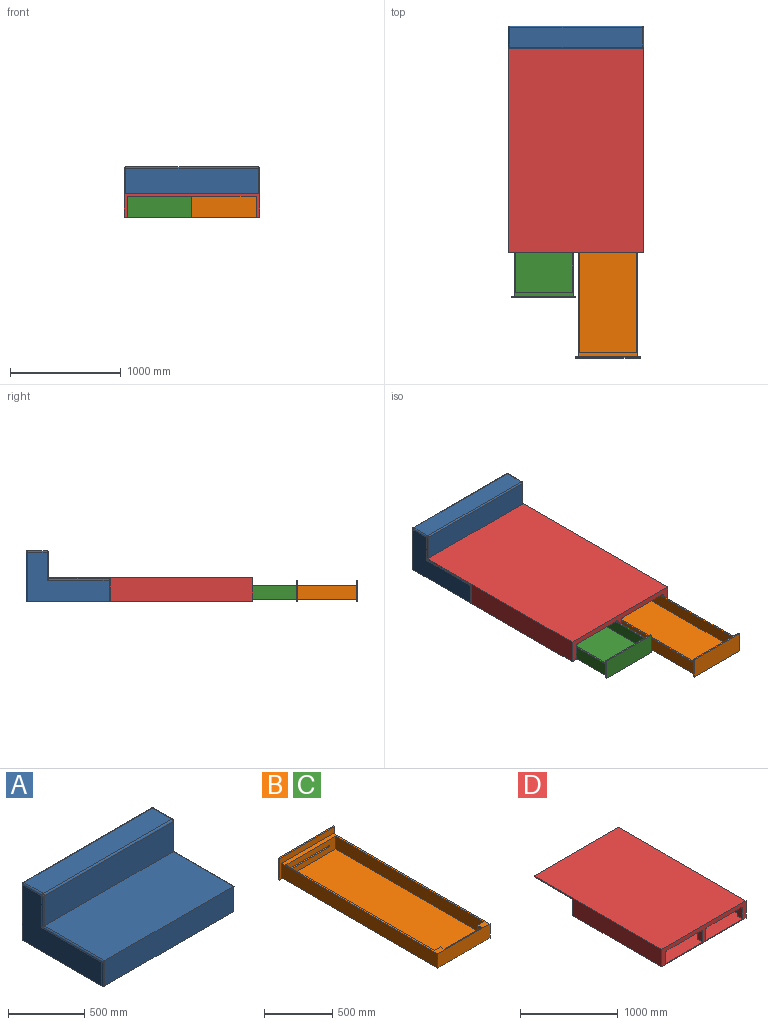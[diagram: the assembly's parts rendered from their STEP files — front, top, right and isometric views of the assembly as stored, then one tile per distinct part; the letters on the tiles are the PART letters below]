
ASSEMBLY  parts=4 mates=6
PART A: 24 faces, bbox 1219.2x762x457.2 mm
  f0: plane 1219.2x762mm, normal (0,0,-1), area 928891.9mm2, adj f1,f5,f6,f7,f8,f9,f17,f20
  f1: plane 1193.8x444.5mm, normal (0,1,0), area 530644.1mm2, adj f0,f17,f20,f23
  f2: plane 1193.8x177.8mm, normal (0,0,1), area 212257.6mm2, adj f13,f18,f19,f23
  f3: plane 1193.8x241.3mm, normal (0,-1,0), area 288063.9mm2, adj f4,f12,f13,f14
  f4: plane 1193.8x558.8mm, normal (0,0,1), area 667095.4mm2, adj f3,f5,f10,f11
  f5: plane 1193.8x203.2mm, normal (0,-1,0), area 242580.2mm2, adj f0,f4,f8,f9
  f6: plane 736.6x444.5mm, normal (1,0,0), area 185483.5mm2, adj f0,f8,f10,f12,f17,f18
  f7: plane 736.6x444.5mm, normal (-1,0,0), area 185483.5mm2, adj f0,f9,f11,f14,f19,f20
  f8: cylinder r=12.7mm len=203.2mm, axis (0,0,1), area 3961.6mm2, adj f0,f5,f6,f10
  f9: cylinder r=12.7mm len=203.2mm, axis (0,0,-1), area 3961.6mm2, adj f0,f5,f7,f11
  f10: cylinder r=12.7mm len=571.5mm, axis (0,1,0), area 11147.6mm2, adj f4,f6,f8,f12
  f11: cylinder r=12.7mm len=571.5mm, axis (0,-1,0), area 11147.6mm2, adj f4,f7,f9,f14
  f12: cylinder r=12.7mm len=254mm, axis (0,0,1), area 4905.8mm2, adj f3,f6,f10,f15
  f13: cylinder r=12.7mm len=1193.8mm, axis (-1,0,0), area 23815.3mm2, adj f2,f3,f15,f16
  f14: cylinder r=12.7mm len=254mm, axis (0,0,-1), area 4905.8mm2, adj f3,f7,f11,f16
  f15: sphere r=12.7mm, area 253.4mm2, adj f12,f13,f18
  f16: sphere r=12.7mm, area 253.4mm2, adj f13,f14,f19
  f17: cylinder r=12.7mm len=444.5mm, axis (0,0,-1), area 8867.4mm2, adj f0,f1,f6,f21
  f18: cylinder r=12.7mm len=177.8mm, axis (0,1,0), area 3547mm2, adj f2,f6,f15,f21
  f19: cylinder r=12.7mm len=177.8mm, axis (0,-1,0), area 3547mm2, adj f2,f7,f16,f22
  f20: cylinder r=12.7mm len=444.5mm, axis (0,0,1), area 8867.4mm2, adj f0,f1,f7,f22
  f21: sphere r=12.7mm, area 253.4mm2, adj f17,f18,f23
  f22: sphere r=12.7mm, area 253.4mm2, adj f19,f20,f23
  f23: cylinder r=12.7mm len=1193.8mm, axis (-1,0,0), area 23815.3mm2, adj f1,f2,f21,f22
PART B: 25 faces, bbox 577.9x1638.3x190.5 mm
  f0: plane 1574.8x514.35mm, normal (0,0,1), area 805159.7mm2, adj f14,f15,f16,f17,f18,f19,f20,f21
  f1: plane 38.1x12.7mm, normal (-1,0,0), area 483.9mm2, adj f4,f14,f23,f24
  f2: plane 38.1x12.7mm, normal (1,0,0), area 483.9mm2, adj f4,f14,f23,f24
  f3: plane 577.85x190.5mm, normal (0,-1,0), area 41532.2mm2, adj f5,f6,f7,f8,f11,f12,f13,f22
  f4: plane 387.35x12.7mm, normal (0,-1,0), area 4919.3mm2, adj f1,f2,f23,f24
  f5: plane 577.85x12.7mm, normal (0,0,1), area 7338.7mm2, adj f3,f6,f8,f9
  f6: plane 190.5x12.7mm, normal (1,0,0), area 2419.4mm2, adj f3,f5,f7,f9
  f7: plane 577.85x12.7mm, normal (0,0,-1), area 7338.7mm2, adj f3,f6,f8,f9
  f8: plane 190.5x12.7mm, normal (-1,0,0), area 2419.4mm2, adj f3,f5,f7,f9
  f9: plane 577.85x190.5mm, normal (0,1,0), area 110080.4mm2, adj f5,f6,f7,f8
  f10: plane 539.75x127mm, normal (0,-1,0), area 68548.2mm2, adj f11,f12,f13,f22
  f11: plane 1625.6x127mm, normal (1,0,0), area 206451.2mm2, adj f3,f10,f13,f22
  f12: plane 1625.6x127mm, normal (-1,0,0), area 206451.2mm2, adj f3,f10,f13,f22
  f13: plane 1625.6x539.75mm, normal (0,0,-1), area 877417.6mm2, adj f3,f10,f11,f12
  f14: plane 514.35x114.3mm, normal (0,-1,0), area 53870.9mm2, adj f0,f1,f2,f15,f21,f22,f23,f24
  f15: plane 1536.7x114.3mm, normal (-1,0,0), area 175644.8mm2, adj f0,f14,f16,f22
  f16: plane 114.3x63.5mm, normal (0,1,0), area 7258.1mm2, adj f0,f15,f17,f22
  f17: plane 114.3x38.1mm, normal (-1,0,0), area 4354.8mm2, adj f0,f16,f18,f22
  f18: plane 387.35x114.3mm, normal (0,1,0), area 44274.1mm2, adj f0,f17,f19,f22
  f19: plane 114.3x38.1mm, normal (1,0,0), area 4354.8mm2, adj f0,f18,f20,f22
  f20: plane 114.3x63.5mm, normal (0,1,0), area 7258mm2, adj f0,f19,f21,f22
  f21: plane 1536.7x114.3mm, normal (1,0,0), area 175644.8mm2, adj f0,f14,f20,f22
  f22: plane 1625.6x539.75mm, normal (0,0,1), area 72257.9mm2, adj f3,f10,f11,f12,f14,f15,f16,f17
  f23: plane 387.35x38.1mm, normal (0,0,-1), area 14758mm2, adj f1,f2,f4,f14
  f24: plane 387.35x38.1mm, normal (0,0,1), area 14758mm2, adj f1,f2,f4,f14
PART C: same geometry as B
PART D: 64 faces, bbox 1219.2x1841.5x215.9 mm
  f0: plane 1104.9x127mm, normal (-1,0,0), area 140322.3mm2, adj f1,f4,f22,f47
  f1: plane 127x38.1mm, normal (0,-1,0), area 4838.7mm2, adj f0,f3,f22,f47
  f2: plane 539.75x152.4mm, normal (0,-1,0), area 82257.9mm2, adj f3,f5,f21,f47
  f3: plane 1270x190.5mm, normal (-1,0,0), area 91357.7mm2, adj f1,f2,f4,f17,f21,f22,f28,f29
  f4: plane 127x38.1mm, normal (0,1,0), area 4838.7mm2, adj f0,f3,f22,f47
  f5: plane 1270x190.5mm, normal (1,0,0), area 91357.7mm2, adj f2,f6,f7,f14,f20,f21,f24,f25
  f6: plane 127x38.1mm, normal (0,-1,0), area 4838.7mm2, adj f5,f13,f14,f47
  f7: plane 127x38.1mm, normal (0,1,0), area 4838.7mm2, adj f5,f13,f14,f47
  f8: plane 1104.9x127mm, normal (1,0,0), area 140322.3mm2, adj f9,f12,f38,f47
  f9: plane 127x38.1mm, normal (0,-1,0), area 4838.7mm2, adj f8,f11,f38,f47
  f10: plane 539.75x152.4mm, normal (0,-1,0), area 82257.9mm2, adj f11,f13,f37,f47
  f11: plane 1270x190.5mm, normal (1,0,0), area 91357.7mm2, adj f9,f10,f12,f33,f37,f38,f44,f45
  f12: plane 127x38.1mm, normal (0,1,0), area 4838.7mm2, adj f8,f11,f38,f47
  f13: plane 1270x190.5mm, normal (-1,0,0), area 91357.7mm2, adj f6,f7,f10,f14,f36,f37,f40,f41
  f14: plane 1104.9x38.1mm, normal (0,0,-1), area 42096.7mm2, adj f5,f6,f7,f13
  f15: plane 477.2x444.16mm, normal (0,0,-1), area 105976mm2, adj f19,f23,f30
  f16: plane 477.2x444.16mm, normal (0,0,-1), area 105976mm2, adj f18,f26,f27
  f17: plane 1009.31x234.86mm, normal (0,0,-1), area 118520.6mm2, adj f3,f28,f29
  f18: plane 444.16x38.1mm, normal (0,-1,0), area 16922.4mm2, adj f16,f21,f26,f27
  f19: plane 444.16x38.1mm, normal (0,1,0), area 16922.4mm2, adj f15,f21,f23,f30
  f20: plane 1009.31x234.86mm, normal (0,0,-1), area 118520.6mm2, adj f5,f24,f25
  f21: plane 1270x539.75mm, normal (0,0,-1), area 235844.3mm2, adj f2,f3,f5,f18,f19,f23,f24,f25
  f22: plane 1104.9x38.1mm, normal (0,0,-1), area 42096.7mm2, adj f0,f1,f3,f4
  f23: plane 477.2x222.08mm, normal (0.91,-0.42,0), area 20053.7mm2, adj f15,f19,f21,f30
  f24: plane 504.65x234.86mm, normal (-0.91,0.42,0), area 21207.4mm2, adj f5,f20,f21,f25
  f25: plane 504.65x234.86mm, normal (-0.91,-0.42,0), area 21207.4mm2, adj f5,f20,f21,f24
  f26: plane 477.2x222.08mm, normal (0.91,0.42,0), area 20053.7mm2, adj f16,f18,f21,f27
  f27: plane 477.2x222.08mm, normal (-0.91,0.42,0), area 20053.7mm2, adj f16,f18,f21,f26
  f28: plane 504.65x234.86mm, normal (0.91,-0.42,0), area 21207.4mm2, adj f3,f17,f21,f29
  f29: plane 504.65x234.86mm, normal (0.91,0.42,0), area 21207.4mm2, adj f3,f17,f21,f28
  f30: plane 477.2x222.08mm, normal (-0.91,-0.42,0), area 20053.7mm2, adj f15,f19,f21,f23
  f31: plane 477.2x444.16mm, normal (0,0,-1), area 105976mm2, adj f35,f39,f46
  f32: plane 477.2x444.16mm, normal (0,0,-1), area 105976mm2, adj f34,f42,f43
  f33: plane 1009.31x234.86mm, normal (0,0,-1), area 118520.6mm2, adj f11,f44,f45
  f34: plane 444.16x38.1mm, normal (0,-1,0), area 16922.4mm2, adj f32,f37,f42,f43
  f35: plane 444.16x38.1mm, normal (0,1,0), area 16922.4mm2, adj f31,f37,f39,f46
  f36: plane 1009.31x234.86mm, normal (0,0,-1), area 118520.6mm2, adj f13,f40,f41
  f37: plane 1270x539.75mm, normal (0,0,-1), area 235844.3mm2, adj f10,f11,f13,f34,f35,f39,f40,f41
  f38: plane 1104.9x38.1mm, normal (0,0,-1), area 42096.7mm2, adj f8,f9,f11,f12
  f39: plane 477.2x222.08mm, normal (-0.91,-0.42,0), area 20053.7mm2, adj f31,f35,f37,f46
  f40: plane 504.65x234.86mm, normal (0.91,0.42,0), area 21207.4mm2, adj f13,f36,f37,f41
  f41: plane 504.65x234.86mm, normal (0.91,-0.42,0), area 21207.4mm2, adj f13,f36,f37,f40
  f42: plane 477.2x222.08mm, normal (-0.91,0.42,0), area 20053.7mm2, adj f32,f34,f37,f43
  f43: plane 477.2x222.08mm, normal (0.91,0.42,0), area 20053.7mm2, adj f32,f34,f37,f42
  f44: plane 504.65x234.86mm, normal (-0.91,-0.42,0), area 21207.4mm2, adj f11,f33,f37,f45
  f45: plane 504.65x234.86mm, normal (-0.91,0.42,0), area 21207.4mm2, adj f11,f33,f37,f44
  f46: plane 477.2x222.08mm, normal (0.91,-0.42,0), area 20053.7mm2, adj f31,f35,f37,f39
  f47: plane 1270x1193.8mm, normal (0,0,1), area 1497255.1mm2, adj f0,f1,f2,f3,f4,f5,f6,f7
  f48: plane 25.4x25.4mm, normal (0,1,0), area 138.5mm2, adj f3,f21,f52
  f49: plane 25.4x25.4mm, normal (0,1,0), area 138.5mm2, adj f11,f37,f53
  f50: plane 25.4x25.4mm, normal (0,1,0), area 138.5mm2, adj f5,f21,f51
  f51: cylinder r=25.4mm len=25.4mm, axis (0,1,0), area 506.7mm2, adj f5,f21,f50,f55
  f52: cylinder r=25.4mm len=25.4mm, axis (0,1,0), area 506.7mm2, adj f3,f21,f48,f55
  f53: cylinder r=25.4mm len=25.4mm, axis (0,1,0), area 506.7mm2, adj f11,f37,f49,f55
  f54: cylinder r=25.4mm len=25.4mm, axis (0,1,0), area 506.7mm2, adj f13,f37,f55,f56
  f55: plane 1219.2x215.9mm, normal (0,-1,0), area 99263.3mm2, adj f3,f5,f11,f13,f21,f37,f47,f51
  f56: plane 25.4x25.4mm, normal (0,1,0), area 138.5mm2, adj f13,f37,f54
  f57: plane 1219.2x558.8mm, normal (0,0,-1), area 681289mm2, adj f58,f59,f61,f63
  f58: plane 1219.2x203.2mm, normal (0,1,0), area 247741.4mm2, adj f57,f61,f62,f63
  f59: plane 1219.2x12.7mm, normal (0,1,0), area 15483.8mm2, adj f57,f60,f61,f63
  f60: plane 1841.5x1219.2mm, normal (0,0,1), area 2245156.8mm2, adj f55,f59,f61,f63
  f61: plane 1841.5x215.9mm, normal (1,0,0), area 284031.7mm2, adj f55,f57,f58,f59,f60,f62
  f62: plane 1282.7x1219.2mm, normal (0,0,-1), area 1563867.8mm2, adj f55,f58,f61,f63
  f63: plane 1841.5x215.9mm, normal (-1,0,0), area 284031.7mm2, adj f55,f57,f58,f59,f60,f62
PLACE A t=(610.18,2044.7,0)mm
PLACE B rot(axis=(0,0,1),180deg) t=(628.65,688.14,12.7)mm
PLACE C rot(axis=(0,0,-1),180deg) t=(50.8,1232.18,12.7)mm
PLACE D t=(609.6,1841.5,0)mm
MATE planar A.f4 <-> D.f57  axis (0,0,1) through (13.28,1562.1,203.2)mm
MATE planar D.f58 <-> A.f5  axis (0,1,0) through (609.6,1282.7,101.6)mm
MATE planar B.f13 <-> D.f47  axis (0,0,-1) through (898.53,-124.66,12.7)mm
MATE planar C.f13 <-> D.f47  axis (0,0,-1) through (320.68,419.38,12.7)mm
MATE planar B.f12 <-> D.f3  axis (1,0,0) through (1168.4,-124.66,76.2)mm
MATE planar C.f11 <-> D.f11  axis (-1,0,0) through (50.8,419.38,76.2)mm
